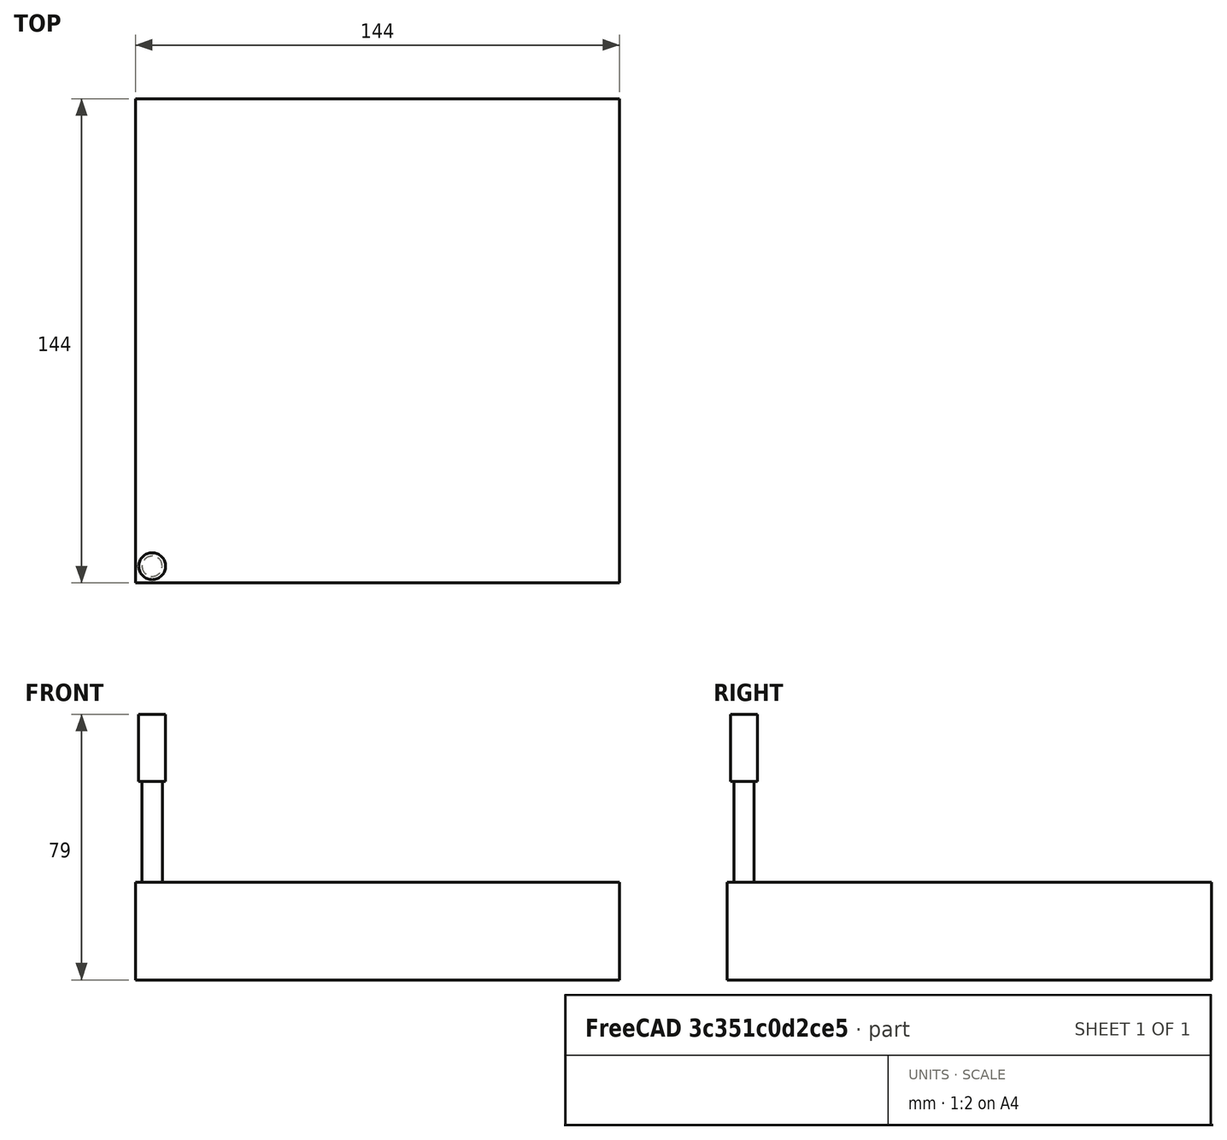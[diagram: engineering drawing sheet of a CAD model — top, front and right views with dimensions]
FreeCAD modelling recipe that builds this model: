
FCSTD DOCUMENT  (FreeCAD 0.22R34789 (Git))
Label: iron_table_insert
License: All rights reserved
LicenseURL: http://en.wikipedia.org/wiki/All_rights_reserved
objects: Path::FeaturePython×6, Part::FeaturePython×4, Sketcher::SketchObject×3, App::DocumentObjectGroup×3, PartDesign::Pocket×2, PartDesign::Pad×1, PartDesign::Body×1, Spreadsheet::Sheet×1, App::FeaturePython×1, Mesh::FeaturePython×1
note: 18 computed .brp shape members not serialized (recipe doc carries the construction recipe); baked Part::Feature solids carry a one-line shape summary decoded from their .brp

FEATURE [Sketcher::SketchObject] Sketch044
  FullyConstrained = true
  MapMode = 5
  Support = -> [XY_Plane019]
  expr: Constraints[16] = Spreadsheet.iron_cast_table / 2
  expr: Constraints[17] = Spreadsheet.iron_cast_table / 2
  expr: Constraints[7] = Spreadsheet.iron_cast_table / 2 - 15 - 2
  expr: Constraints[8] = Spreadsheet.iron_cast_table / 2 - 15 - 2
  sketch-geometry (7):
    g0: GeomPoint X=131 Y=131 Z=0
    g1: LineSegment StartX=5 StartY=5 StartZ=0 EndX=119 EndY=5 EndZ=0
    g2: LineSegment StartX=119 StartY=5 StartZ=0 EndX=119 EndY=81 EndZ=0
    g3: LineSegment StartX=81 StartY=119 StartZ=0 EndX=5 EndY=119 EndZ=0
    g4: LineSegment StartX=5 StartY=119 StartZ=0 EndX=5 EndY=5 EndZ=0
    g5: ArcOfCircle CenterX=81 CenterY=81 CenterZ=0 NormalX=0 NormalY=0 NormalZ=1 AngleXU=0 Radius=38 StartAngle=8e-16 EndAngle=1.5708
    g6: GeomPoint X=119 Y=119 Z=0
  constraints (18):
    c: Coincident(g1,g2)
    c: Coincident(g3,g4)
    c: Coincident(g4,g1)
    c: Horizontal(g1)
    c: Horizontal(g3)
    c: Vertical(g2)
    c: Vertical(g4)
    c: DistanceY(g4,g4) = 114
    c: DistanceX(g1,g1) = 114
    c: PointOnObject(g6,g3)
    c: PointOnObject(g6,g2)
    c: Tangent(g3,g5) = -1.5708
    c: Tangent(g2,g5) = -1.5708
    c: Radius(g5) = 38
    c: DistanceX(g-1,g1) = 5
    c: DistanceY(g-1,g1) = 5
    c: DistanceY(g0) = 131
    c: DistanceX(g0) = 131
FEATURE [PartDesign::Pad] Pad016
  Direction = (0,0,1)
  Length = 24
  Length2 = 10
  Profile = -> Sketch044
  ReferenceAxis = -> Sketch044 [N_Axis]
  Type = 0
  expr: Length = 2 * Spreadsheet.ply_12
FEATURE [Sketcher::SketchObject] Sketch045
  FullyConstrained = false
  MapMode = 5
  Placement = pos=(0,0,0) rot=(1,0,0;3.14159rad)
  Support = -> [Pad016]
  sketch-geometry (5):
    g0: LineSegment StartX=12.3744 StartY=12.3744 StartZ=0 EndX=123.206 EndY=-98.4574 EndZ=0
    g1: LineSegment StartX=-12.3744 StartY=-12.3744 StartZ=0 EndX=98.4574 EndY=-123.206 EndZ=0
    g2: LineSegment StartX=0 StartY=0 StartZ=0 EndX=12.3744 EndY=12.3744 EndZ=0
    g3: LineSegment StartX=0 StartY=0 StartZ=0 EndX=-12.3744 EndY=-12.3744 EndZ=0
    g4: LineSegment StartX=98.4574 StartY=-123.206 StartZ=0 EndX=123.206 EndY=-98.4574 EndZ=0
  constraints (6):
    c: Perpendicular(g2,g0) = 4.71239
    c: Perpendicular(g3,g1) = 1.5708
    c: Coincident(g0,g4)
    c: Coincident(g4,g1)
    c: Distance(g-1,g0) = 17.5
    c: Distance(g1,g-1) = 17.5
FEATURE [PartDesign::Pocket] Pocket028
  BaseFeature = -> Pad016
  Direction = (0,0,1)
  Length = 5
  Length2 = 5
  Profile = -> Sketch045
  ReferenceAxis = -> Sketch045 [N_Axis]
  Type = 0
FEATURE [Sketcher::SketchObject] Sketch046
  FullyConstrained = true
  MapMode = 5
  Placement = pos=(0,0,24) rot=(0,0,1;0rad)
  Support = -> [Pocket028]
  expr: Constraints[2] = 12 mm
  expr: Constraints[3] = Spreadsheet.mounting_screws_distance / 2
  expr: Constraints[4] = Spreadsheet.mounting_screws_distance / 2
  sketch-geometry (2):
    g0: Circle CenterX=0 CenterY=0 CenterZ=0 NormalX=0 NormalY=0 NormalZ=1 AngleXU=0 Radius=32
    g1: Circle CenterX=85 CenterY=85 CenterZ=0 NormalX=0 NormalY=0 NormalZ=1 AngleXU=0 Radius=6
  constraints (5):
    c: Coincident(g0,g-1)
    c: Diameter(g0) = 64
    c: Diameter(g1) = 12
    c: DistanceX(g0,g1) = 85
    c: DistanceY(g0,g1) = 85
FEATURE [PartDesign::Pocket] Pocket029
  BaseFeature = -> Pocket028
  Direction = (0,0,-1)
  Length = 24
  Length2 = 5
  Profile = -> Sketch046
  ReferenceAxis = -> Sketch046 [N_Axis]
  Type = 0
FEATURE [PartDesign::Body] Body014  label="iron_table_insert"
  Group = -> [Sketch044,Pad016,Sketch045,Pocket028,Sketch046,Pocket029]
  Origin = -> Origin018
  Placement = pos=(0,0,0) rot=(1,0,0;3.14159rad)
  Tip = -> Pocket029
FEATURE [Spreadsheet::Sheet] Spreadsheet
  cells = A1='table_length; B1(table_length)=720; D1='plywood_18; E1(ply_18)=18; F1='iron_cast_table; G1(iron_cast_table)=262; I1='nakrętka kłowa M8 DIN1624; L1='otwory_przelotowe; A2='table_depth; B2(table_depth)=420; D2='plywood_12; E2(ply_12)=12; F2='mounting_screws_distance; G2(mounting_screws_distance)=170; I2='M8_D; J2(DIN1624_M8_D)=22.2; L2='M8_D; M2(otw_przel_M8)=8.4; D3='plywood_3; E3(ply_3)=3; I3='M8_d1; J3(DIN1624_M8_d1)=9.1; A4='table_radius; B4(table_radius)=6; I4='M8_a; J4(DIN1624_M8_a)=1.2; I5='M8_L1; J5(DIN1624_M8_L1)=11; A6='t_track_slim_width; B6(t_track_width)=19; C6='https://allegro.pl/oferta/t-track-slim-1220mm-profil-aluminiowy-t-zielony-10608302634?fromVariant=12640372726; A7='t_track_slim_depth; B7(t_track_depth)=9.5; D7='fence_base_d; E7(fence_base_d)=32; I7='M10_D; J7(DIN1624_M10_D)=25.5; D8='fence_face_d; E8(fence_face_d)=32; I8='M10_d1; J8(DIN1624_M10_d1)=12; A9='clamp_slot_width; B9(clamp_slot_width)=32; I9='M10_a; J9(DIN1624_M10_a)=1.2; I10='M10_L1; J10(DIN1624_M10_L1)=13; A11='insert_width; B11(insert_width)=90; D11='base_width; E11(base_width)==G1; A12='insert_depth; B12(insert_depth)=200; D12='base_depth; E12(base_depth)==E1 + 60 + E2 + E15 + 10; I12='M12_D; J12(DIN1624_M12_D)=27; D13='base_height; E13(base_height)=75; I13='M12_d1; J13(DIN1624_M12_d1)=13.7; I14='M12_a; J14(DIN1624_M12_a)=1.6; D15='drawer_depth; E15(drawer_depth)=200; I15='M12_L1; J15(DIN1624_M12_L1)=14.5; D16='drawer_slide_width; E16=12.7; D17='drawer_total_depth; E17(drawer_total_depth)==E15 + 6; D18='drawer_total_width; E18(drawer_total_width)==E11 - 2 * E1 - 2 * E16; D19='drawer_total_height; E19(drawer_total_height)==E13 - E1 - 9
FEATURE [App::FeaturePython] SetupSheet  # Path/CAM operation (typed FeaturePython)
  ClearanceHeightExpression = OpStockZMax+SetupSheet.ClearanceHeightOffset
  ClearanceHeightOffset = 5
  CoolantMode = 0
  CoolantModes = None | Flood | Mist
  FinalDepthExpression = OpFinalDepth
  HorizRapid = 0
  SafeHeightExpression = OpStockZMax+SetupSheet.SafeHeightOffset
  SafeHeightOffset = 3
  StartDepthExpression = OpStartDepth
  StepDownExpression = OpToolDiameter/3
  VertRapid = 0
FEATURE [Part::FeaturePython] Clone  label="Model-iron_table_insert"  # Draft clone (typed FeaturePython)
  AttacherType = Attacher::AttachEngine3D
  Fuse = false
  Objects = -> [Body014]
  PathResource = Model
  Placement = pos=(5,129,-1.4e-14) rot=(1,0,0;3.14159rad)
  Scale = (1,1,1)
FEATURE [App::DocumentObjectGroup] Model
  Group = -> [Clone]
FEATURE [Part::FeaturePython] Stock  # WARN: FeaturePython — macro-defined, semantics opaque (R4)
  Base = -> Model
  ExtXneg = 15
  ExtXpos = 15
  ExtYneg = 15
  ExtYpos = 15
  ExtZneg = 5
  ExtZpos = 0
  Placement = pos=(10,10,-24) rot=(0,0,1;0rad)
  StockType = FromBase
FEATURE [Part::FeaturePython] ToolBit001  label="6 mm endmill"  # Path/CAM toolbit (typed FeaturePython)
  BitPropertyNames = Chipload | CuttingEdgeHeight | Diameter | Flutes | Length | Material | ShankDiameter | SpindleDirection
  BitShape = <userpath>/.local/share/FreeCAD/Macro/Tools/Shape/endmill.fcstd
  Chipload = 0
  CuttingEdgeHeight = 30
  Diameter = 6
  File = <userpath>/.local/share/FreeCAD/Macro/Tools/Bit/fbe41074-7b3e-11ee-b334-02422c3495f2.fctb
  Flutes = 2
  Length = 50
  Material = 0
  ShankDiameter = 8
  ShapeName = endmill
  SpindleDirection = 0
FEATURE [Part::FeaturePython] ToolBit  label="6 mm endmill001"  # Path/CAM toolbit (typed FeaturePython)
  BitPropertyNames = Chipload | CuttingEdgeHeight | Diameter | Flutes | Length | Material | ShankDiameter | SpindleDirection
  BitShape = <path>
  Chipload = 0
  CuttingEdgeHeight = 30
  Diameter = 6
  Flutes = 2
  Length = 50
  Material = 0
  ShankDiameter = 8
  ShapeName = endmill
  SpindleDirection = 0
FEATURE [Path::FeaturePython] TC__6_mm_endmill  label="TC: 6 mm endmill"  # Path/CAM operation (typed FeaturePython)
  HorizFeed = 10
  HorizRapid = 0
  SpindleDir = 0
  SpindleSpeed = 0
  Tool = -> ToolBit
  ToolNumber = 16
  VertFeed = 1
  VertRapid = 0
  expr: HorizRapid = SetupSheet.HorizRapid
  expr: VertRapid = SetupSheet.VertRapid
FEATURE [App::DocumentObjectGroup] Tools
  Group = -> [TC__6_mm_endmill]
FEATURE [Path::FeaturePython] Profile001  # Path/CAM operation (typed FeaturePython)
  Active = true
  AreaParams:
    Tolerance = 1e-07
    FitArcs = True
    Simplify = False
    CleanDistance = 0.0
    Accuracy = 0.01
    Unit = 1.0
    MinArcPoints = 4
    MaxArcPoints = 100
    ClipperScale = 10000000.0
    Fill = 0
    Coplanar = 0
    Reorient = True
    Outline = False
    Explode = False
    OpenMode = 0
    Deflection = 0.01
    SubjectFill = 0
    ClipFill = 0
    Offset = -3.5
    ExtraPass = 0
    Stepover = 0.0
    LastStepover = 0.0
    JoinType = 0
    EndType = 0
    MiterLimit = 2.0
    RoundPrecision = 0.0
    PocketMode = 0
    ToolRadius = 1.0
    PocketExtraOffset = 0.0
    PocketStepover = 0.0
    PocketLastStepover = 0.0
    FromCenter = False
    Angle = 45.0
    AngleShift = 0.0
    Shift = 0.0
    Thicken = False
    SectionCount = -1
    Stepdown = 1.0
    SectionOffset = 0.0
    SectionTolerance = 1e-07
    SectionMode = 2
    Project = False
  Base = -> [Clone]
  ClearanceHeight = 5
  CoolantMode = 0
  CycleTime = 00:01:38
  Direction = 0
  FinalDepth = -29
  HandleMultipleFeatures = 0
  JoinType = 0
  MiterLimit = 0.1
  OffsetExtra = 0.5
  OpFinalDepth = -24
  OpStartDepth = 0
  OpStockZMax = -1.42e-14
  OpStockZMin = -29
  OpToolDiameter = 6
  PathParams = {'orientation': 1, 'feedrate': 10.0, 'feedrate_v': 1.0, 'verbose': True, 'resume_height': 2.999999999999986, 'retraction': 4.999999999999986, 'return_end': True, 'preamble': False}
  SafeHeight = 3
  Side = 1
  SplitArcs = false
  StartDepth = 0
  StartPoint = (0,0,0)
  StepDown = 2
  ToolController = -> TC__6_mm_endmill
  UseComp = true
  UseStartPoint = false
  processCircles = false
  processHoles = false
  processPerimeter = true
  expr: ClearanceHeight = OpStockZMax + SetupSheet.ClearanceHeightOffset
  expr: FinalDepth = OpFinalDepth - 5 mm
  expr: SafeHeight = OpStockZMax + SetupSheet.SafeHeightOffset
  expr: StartDepth = OpStartDepth
  expr: StepDown = OpToolDiameter / 3
FEATURE [Path::FeaturePython] Pocket_Shape  # Path/CAM operation (typed FeaturePython)
  Active = true
  AreaParams:
    Tolerance = 1e-07
    FitArcs = True
    Simplify = False
    CleanDistance = 0.0
    Accuracy = 0.01
    Unit = 1.0
    MinArcPoints = 4
    MaxArcPoints = 100
    ClipperScale = 10000000.0
    Fill = 0
    Coplanar = 0
    Reorient = True
    Outline = False
    Explode = False
    OpenMode = 0
    Deflection = 0.01
    SubjectFill = 0
    ClipFill = 0
    Offset = 0.0
    ExtraPass = 0
    Stepover = 0.0
    LastStepover = 0.0
    JoinType = 0
    EndType = 0
    MiterLimit = 2.0
    RoundPrecision = 0.0
    PocketMode = 2
    ToolRadius = 3.0
    PocketExtraOffset = 0.0
    PocketStepover = 4.800000000000001
    PocketLastStepover = 0.0
    FromCenter = True
    Angle = 45.0
    AngleShift = 0.0
    Shift = 0.0
    Thicken = False
    SectionCount = -1
    Stepdown = 1.0
    SectionOffset = 0.0
    SectionTolerance = 1e-07
    SectionMode = 2
    Project = False
  Base = -> [Clone]
  ClearanceHeight = 5
  CoolantMode = 0
  CutMode = 0
  CycleTime = 00:07:51
  ExtensionCorners = true
  ExtensionFeature = -> [Clone]
  ExtensionLengthDefault = 3
  ExtraOffset = 0
  FinalDepth = -5.5
  FinishDepth = 0
  KeepToolDown = false
  MinTravel = false
  OffsetPattern = 1
  OpFinalDepth = -5
  OpStartDepth = 4e-16
  OpStockZMax = -1.42e-14
  OpStockZMin = -29
  OpToolDiameter = 6
  PathParams = {'orientation': 1, 'feedrate': 10.0, 'feedrate_v': 1.0, 'verbose': True, 'resume_height': 2.999999999999986, 'retraction': 4.999999999999986, 'return_end': True, 'preamble': False}
  PocketLastStepOver = 0
  SafeHeight = 3
  SplitArcs = false
  StartAt = 0
  StartDepth = 4e-16
  StartPoint = (0,0,0)
  StepDown = 2
  StepOver = 80
  ToolController = -> TC__6_mm_endmill
  UseOutline = true
  UseRestMachining = false
  UseStartPoint = false
  ZigZagAngle = 45
  expr: ClearanceHeight = OpStockZMax + SetupSheet.ClearanceHeightOffset
  expr: ExtensionLengthDefault = OpToolDiameter / 2
  expr: FinalDepth = OpFinalDepth - 0.5 mm
  expr: SafeHeight = OpStockZMax + SetupSheet.SafeHeightOffset
  expr: StartDepth = OpStartDepth
  expr: StepDown = OpToolDiameter / 3
FEATURE [Path::FeaturePython] Profile  # Path/CAM operation (typed FeaturePython)
  Active = true
  AreaParams:
    Tolerance = 1e-07
    FitArcs = True
    Simplify = False
    CleanDistance = 0.0
    Accuracy = 0.01
    Unit = 1.0
    MinArcPoints = 4
    MaxArcPoints = 100
    ClipperScale = 10000000.0
    Fill = 0
    Coplanar = 0
    Reorient = True
    Outline = False
    Explode = False
    OpenMode = 0
    Deflection = 0.01
    SubjectFill = 0
    ClipFill = 0
    Offset = 3.0
    ExtraPass = 0
    Stepover = 0.0
    LastStepover = 0.0
    JoinType = 0
    EndType = 0
    MiterLimit = 2.0
    RoundPrecision = 0.0
    PocketMode = 0
    ToolRadius = 1.0
    PocketExtraOffset = 0.0
    PocketStepover = 0.0
    PocketLastStepover = 0.0
    FromCenter = False
    Angle = 45.0
    AngleShift = 0.0
    Shift = 0.0
    Thicken = False
    SectionCount = -1
    Stepdown = 1.0
    SectionOffset = 0.0
    SectionTolerance = 1e-07
    SectionMode = 2
    Project = False
  ClearanceHeight = 5
  CoolantMode = 0
  CycleTime = 00:11:22
  Direction = 0
  FinalDepth = -29
  HandleMultipleFeatures = 0
  JoinType = 0
  MiterLimit = 0.1
  OffsetExtra = 0
  OpFinalDepth = -29
  OpStartDepth = -1.42e-14
  OpStockZMax = -1.42e-14
  OpStockZMin = -29
  OpToolDiameter = 6
  PathParams = {'orientation': 1, 'feedrate': 10.0, 'feedrate_v': 1.0, 'verbose': True, 'resume_height': 2.999999999999986, 'retraction': 4.999999999999986, 'return_end': True, 'preamble': False}
  SafeHeight = 3
  Side = 0
  SplitArcs = false
  StartDepth = -1.42e-14
  StartPoint = (0,0,0)
  StepDown = 2
  ToolController = -> TC__6_mm_endmill
  UseComp = true
  UseStartPoint = false
  processCircles = false
  processHoles = false
  processPerimeter = true
  expr: ClearanceHeight = OpStockZMax + SetupSheet.ClearanceHeightOffset
  expr: FinalDepth = OpFinalDepth
  expr: SafeHeight = OpStockZMax + SetupSheet.SafeHeightOffset
  expr: StartDepth = OpStartDepth
  expr: StepDown = OpToolDiameter / 3
FEATURE [Path::FeaturePython] DressupTag  # Path/CAM operation (typed FeaturePython)
  Angle = 45
  Base = -> Profile
  Height = 14
  Positions = (2) [(7,53.6965,0),(127,86,0)]
  Radius = 0
  SegmentationFactor = 50
  Width = 10
FEATURE [App::DocumentObjectGroup] Operations
  Group = -> [Profile001,Pocket_Shape,DressupTag]
FEATURE [Path::FeaturePython] Job  # Path/CAM operation (typed FeaturePython)
  CycleTime = 00:20:51
  Fixtures = G54
  GeometryTolerance = 0.01
  JobType = 0
  LastPostProcessDate = 2023-11-07 11:11:36.300993
  LastPostProcessOutput = <userpath>/projekty/woodworking/drill_press/cnc/iron_table_insert.gcode
  Model = -> Model
  Operations = -> Operations
  OrderOutputBy = 0
  PostProcessor = 1
  SetupSheet = -> SetupSheet
  SplitOutput = false
  Stock = -> Stock
  Tools = -> Tools
FEATURE [Mesh::FeaturePython] CutMaterial  # WARN: FeaturePython — macro-defined, semantics opaque (R4)
note: 1 file-system path scrubbed to <path> (originals preserved in the JSON sidecar)
